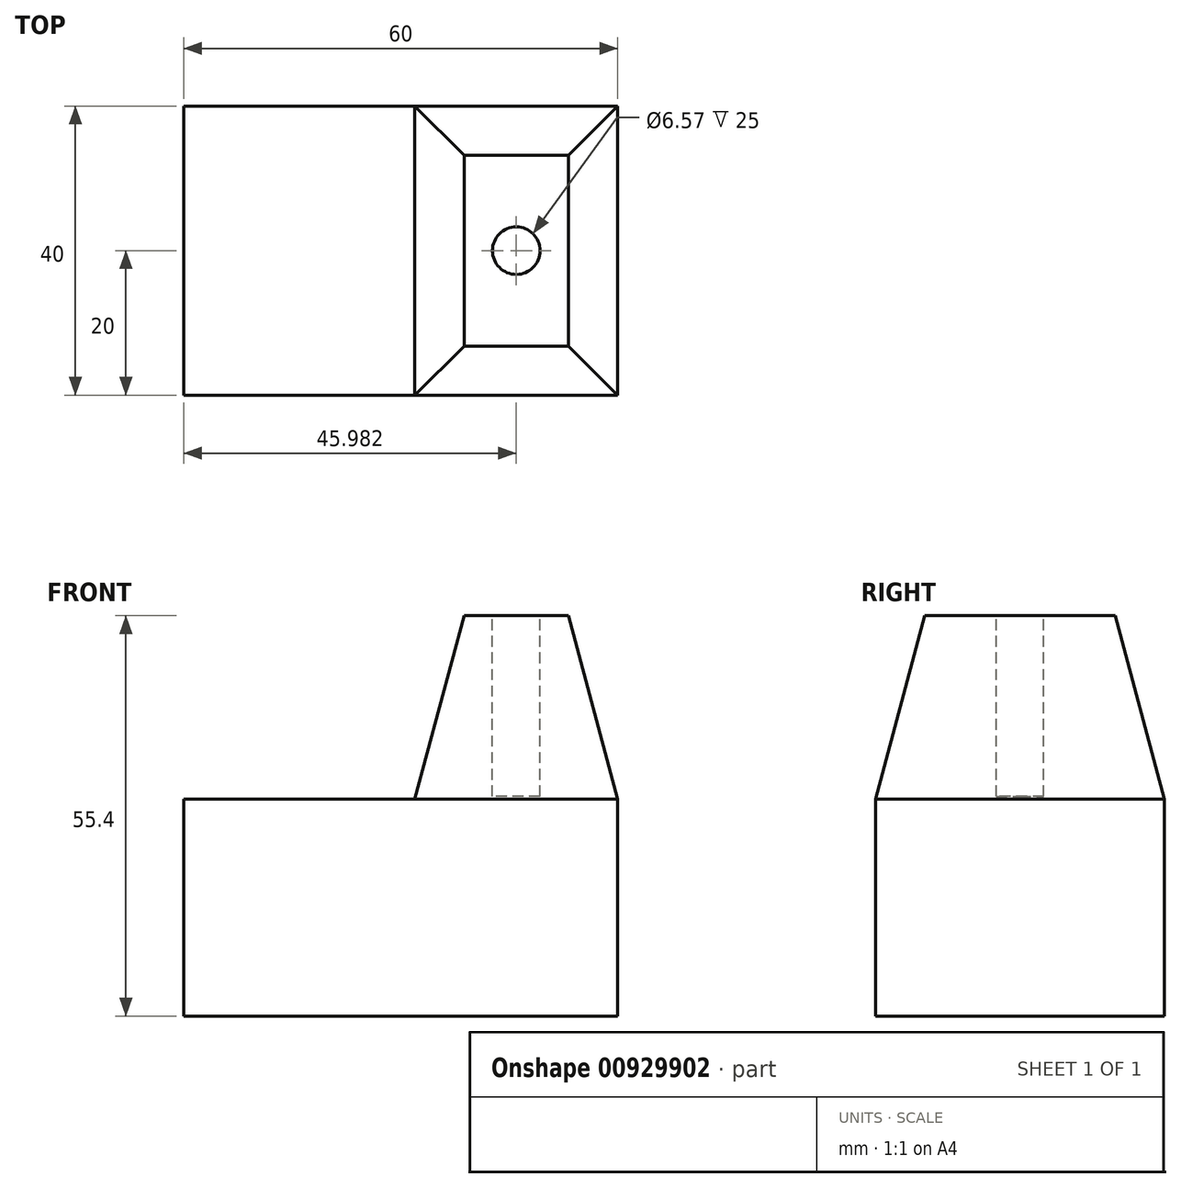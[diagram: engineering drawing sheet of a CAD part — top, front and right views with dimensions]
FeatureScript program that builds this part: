
annotation { "Feature Type Name" : "Feature", "Feature Type Description" : "" }
export const myFeature = defineFeature(function(context is Context, id is Id, definition is map)
    precondition{}
    {
        {
            var Q0;
            Q0=qCreatedBy(makeId("Front.planeOp"),FACE);
            var sketch = newSketch(context, id + "F0", { "sketchPlane" : qUnion([Q0])});
            skLineSegment(sketch, "E0.bottom", {"start": v(-31.96, 23.16) * mm, "end": v(28.04, 23.16) * mm});
            skLineSegment(sketch, "E0.top", {"start": v(-31.96, -6.84) * mm, "end": v(28.04, -6.84) * mm});
            skLineSegment(sketch, "E0.left", {"start": v(-31.96, 23.16) * mm, "end": v(-31.96, -6.84) * mm});
            skLineSegment(sketch, "E0.right", {"start": v(28.04, 23.16) * mm, "end": v(28.04, -6.84) * mm});
            skSolve(sketch);
        }
        {
            var Q0;
            Q0=makeQuery(id+"F0.imprint","IMPRINT",FACE,{"disambiguationData":[TD([[makeQuery(id+"F0.imprint","IMPRINT",EDGE,{"derivedFrom":sQuery(id+"F0.wireOp",EDGE,"E0.bottom")}),-1.0]])]});
            var Q1;
            Q1 = qSketchRegion(id + "FYZoyMcfqwc6VAR_1", true);
            extrude(context, id + "F1", {"entities" : qUnion([Q0, Q1]), "depth" : 40 * mm, "offsetDistance" : 25.4 * mm});
        }
        {
            var Q0;
            Q0=makeQuery(id+"F1.opExtrude","SWEPT_FACE",FACE,{"disambiguationData":[OSD([sQuery(id+"F0.wireOp",EDGE,"E0.bottom")])]});
            var sketch = newSketch(context, id + "F2", { "sketchPlane" : qUnion([Q0])});
            skLineSegment(sketch, "E1.bottom", {"start": v(0, 0) * mm, "end": v(28.04, 0) * mm});
            skLineSegment(sketch, "E1.top", {"start": v(0, -40) * mm, "end": v(28.04, -40) * mm});
            skLineSegment(sketch, "E1.left", {"start": v(0, 0) * mm, "end": v(0, -40) * mm});
            skLineSegment(sketch, "E1.right", {"start": v(28.04, 0) * mm, "end": v(28.04, -40) * mm});
            skSolve(sketch);
        }
        {
            var Q0;
            Q0=makeQuery(id+"F2.imprint","IMPRINT",FACE,{"disambiguationData":[TD([[makeQuery(id+"F2.imprint","IMPRINT",EDGE,{"derivedFrom":sQuery(id+"F2.wireOp",EDGE,"E1.bottom")}),-1.0]])]});
            extrude(context, id + "F3", {"entities" : qUnion([Q0]), "operationType" : NewBodyOperationType.ADD, "depth" : 25.4 * mm, "offsetDistance" : 25.4 * mm, "hasDraft" : true, "draftAngle" : 15 * degree, "draftPullDirection" : true});
        }
        {
            var Q0;
            Q0=makeQuery(id+"F3.opExtrude","CAP_FACE",FACE,{"disambiguationData":[OSD([sQuery(id+"F2.wireOp",EDGE,"E1.bottom"),sQuery(id+"F2.wireOp",EDGE,"E1.top"),sQuery(id+"F2.wireOp",EDGE,"E1.left"),sQuery(id+"F2.wireOp",EDGE,"E1.right")])],"isStart":false});
            var sketch = newSketch(context, id + "F4", { "sketchPlane" : qUnion([Q0])});
            skCircle(sketch, "E2", {"center": v(14.02, -20) * mm, "radius": 3.29 * mm});
            skPoint(sketch, "E2.centerSnap0", {"position": v(14.02, -6.8) * mm});
            skPoint(sketch, "E2.centerSnap1", {"position": v(21.24, -20) * mm});
            skSolve(sketch);
        }
        {
            var Q0;
            Q0=makeQuery(id+"F4.imprint","IMPRINT",FACE,{"disambiguationData":[TD([[makeQuery(id+"F4.imprint","IMPRINT",EDGE,{"derivedFrom":sQuery(id+"F4.wireOp",EDGE,"E2")}),1.0]])]});
            extrude(context, id + "F5", {"entities" : qUnion([Q0]), "operationType" : NewBodyOperationType.REMOVE, "oppositeDirection" : true, "depth" : 25 * mm, "offsetDistance" : 25.4 * mm});
        }
    });
